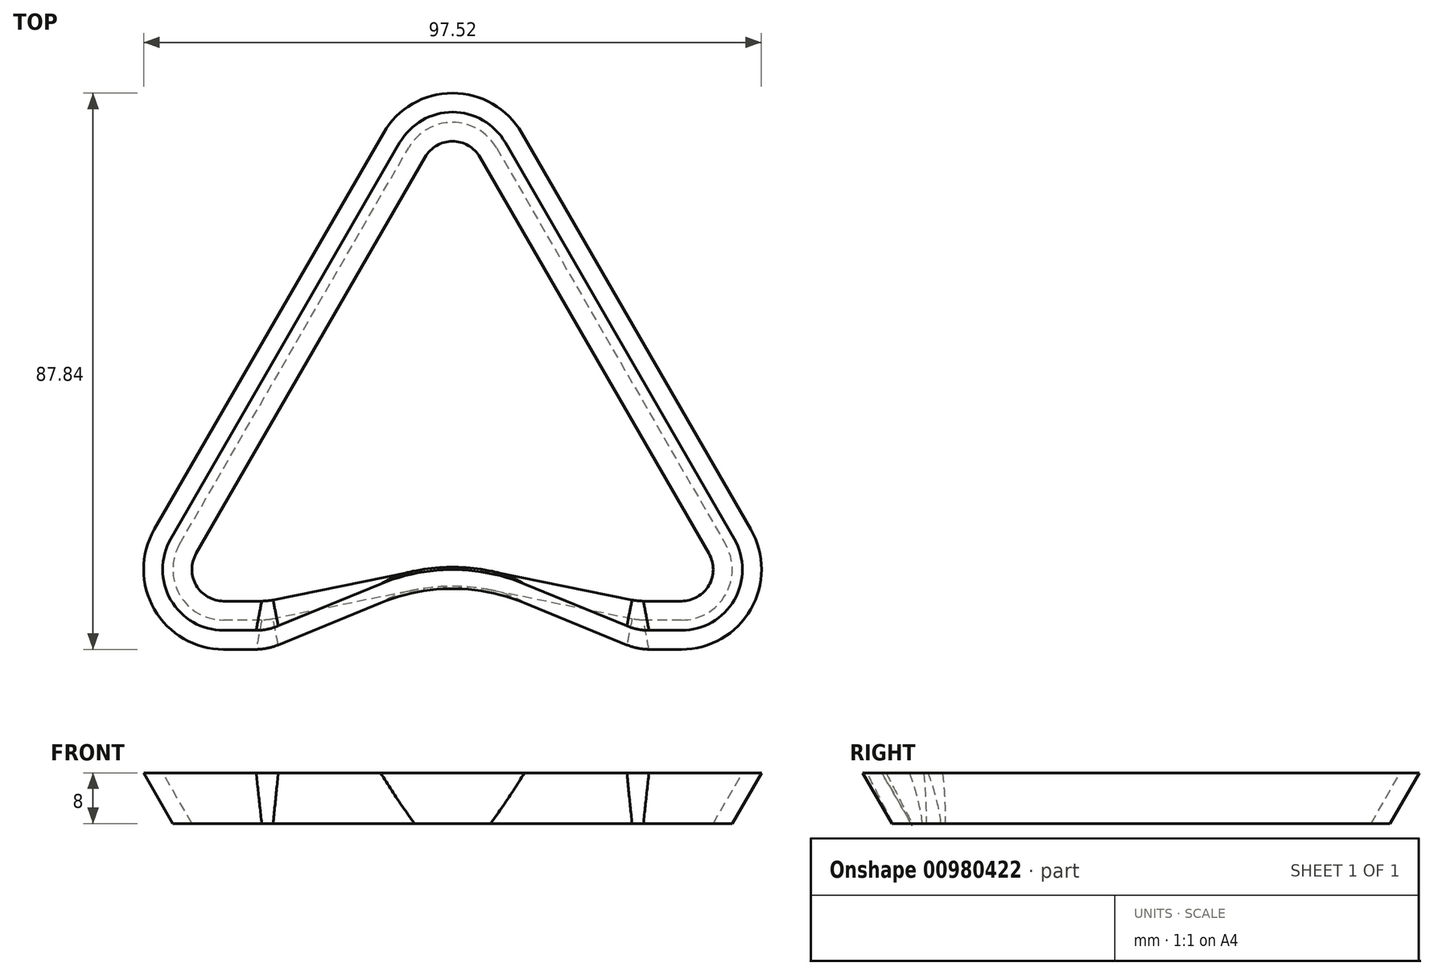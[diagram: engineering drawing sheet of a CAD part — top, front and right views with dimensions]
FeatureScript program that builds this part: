
annotation { "Feature Type Name" : "Feature", "Feature Type Description" : "" }
export const myFeature = defineFeature(function(context is Context, id is Id, definition is map)
    precondition{}
    {
        {
            var Q0;
            Q0=qCreatedBy(makeId("Top.planeOp"),FACE);
            var sketch = newSketch(context, id + "F0", { "sketchPlane" : qUnion([Q0])});
            skLineSegment(sketch, "E0", {"start": v(-50, 0) * mm, "end": v(50, 0) * mm, "construction": true});
            skLineSegment(sketch, "E1", {"start": v(50, 0) * mm, "end": v(0, 86.6) * mm, "construction": true});
            skLineSegment(sketch, "E2", {"start": v(0, 86.6) * mm, "end": v(-50, 0) * mm, "construction": true});
            skArc(sketch, "E3", {"start": v(-43.07, 12) * mm, "mid": v(-43.07, 4) * mm, "end": v(-36.14, 0) * mm});
            skArc(sketch, "E4", {"start": v(36.14, 0) * mm, "mid": v(43.07, 4) * mm, "end": v(43.07, 12) * mm});
            skArc(sketch, "E5", {"start": v(6.93, 74.6) * mm, "mid": v(0, 78.6) * mm, "end": v(-6.93, 74.6) * mm});
            skLineSegment(sketch, "E6", {"start": v(-43.07, 12) * mm, "end": v(-6.93, 74.6) * mm});
            skLineSegment(sketch, "E7", {"start": v(6.93, 74.6) * mm, "end": v(43.07, 12) * mm});
            skLineSegment(sketch, "E8", {"start": v(-36.14, 0) * mm, "end": v(-29.23, 0) * mm});
            skLineSegment(sketch, "E9", {"start": v(29.23, 0) * mm, "end": v(36.14, 0) * mm});
            skArc(sketch, "E10", {"start": v(3.3, 11.28) * mm, "mid": v(0, 12) * mm, "end": v(-3.3, 11.28) * mm});
            skLineSegment(sketch, "E11", {"start": v(-27.16, 0.45) * mm, "end": v(-3.3, 11.28) * mm});
            skLineSegment(sketch, "E12", {"start": v(3.3, 11.28) * mm, "end": v(27.16, 0.45) * mm});
            skPoint(sketch, "E13.visualSharp", {"position": v(-28.14, 0) * mm});
            skArc(sketch, "E13.filletArc", {"start": v(-29.23, 0) * mm, "mid": v(-28.17, 0.11) * mm, "end": v(-27.16, 0.45) * mm});
            skPoint(sketch, "E14.visualSharp", {"position": v(28.14, 0) * mm});
            skArc(sketch, "E14.filletArc", {"start": v(27.16, 0.45) * mm, "mid": v(28.17, 0.11) * mm, "end": v(29.23, 0) * mm});
            skLineSegment(sketch, "E15", {"start": v(-29.23, 0) * mm, "end": v(-29.23, 8) * mm, "construction": true});
            skSolve(sketch);
        }
        {
            var Q0;
            Q0=qCreatedBy(makeId("Right.planeOp"),FACE);
            var sketch = newSketch(context, id + "F1", { "sketchPlane" : qUnion([Q0])});
            skPoint(sketch, "E16.0", {"position": v(12, 0) * mm});
            skLineSegment(sketch, "E17", {"start": v(15, 0) * mm, "end": v(10.38, 8) * mm});
            skLineSegment(sketch, "E18", {"start": v(10.38, 8) * mm, "end": v(7.38, 8) * mm});
            skLineSegment(sketch, "E19", {"start": v(7.38, 8) * mm, "end": v(12, 0) * mm});
            skLineSegment(sketch, "E20", {"start": v(12, 0) * mm, "end": v(15, 0) * mm});
            skSolve(sketch);
        }
        {
            var Q0;
            Q0=sQuery(id+"F0.wireOp",EDGE,"E15");
            cPlane(context, id + "F2", {"entities" : qUnion([Q0]), "cplaneType" : CPlaneType.LINE_ANGLE, "offset" : 25 * mm, "angle" : 90 * degree, "width" : 150 * mm, "height" : 150 * mm});
        }
        {
            var Q0;
            Q0=qCreatedBy(id+"F2.planeOp",FACE);
            var sketch = newSketch(context, id + "F3", { "sketchPlane" : qUnion([Q0])});
            skLineSegment(sketch, "E21", {"start": v(0, 0) * mm, "end": v(-4.62, 8) * mm});
            skLineSegment(sketch, "E22", {"start": v(-4.62, 8) * mm, "end": v(-1.62, 8) * mm});
            skLineSegment(sketch, "E23", {"start": v(-1.62, 8) * mm, "end": v(3, 0) * mm});
            skLineSegment(sketch, "E24", {"start": v(3, 0) * mm, "end": v(0, 0) * mm});
            skSolve(sketch);
        }
        {
            var Q0;
            Q0=makeQuery(id+"F3.imprint","IMPRINT",FACE,{"disambiguationData":[TD([[makeQuery(id+"F3.imprint","IMPRINT",EDGE,{"derivedFrom":sQuery(id+"F3.wireOp",EDGE,"E21")}),-1.0]])]});
            var Q1;
            Q1=sQuery(id+"F0.wireOp",EDGE,"E8");
            var Q2;
            Q2=sQuery(id+"F0.wireOp",EDGE,"E3");
            var Q3;
            Q3=sQuery(id+"F0.wireOp",EDGE,"E6");
            var Q4;
            Q4=sQuery(id+"F0.wireOp",EDGE,"E5");
            var Q5;
            Q5=sQuery(id+"F0.wireOp",EDGE,"E7");
            var Q6;
            Q6=sQuery(id+"F0.wireOp",EDGE,"E4");
            var Q7;
            Q7=sQuery(id+"F0.wireOp",EDGE,"E9");
            sweep(context, id + "F4", {"profiles" : qUnion([Q0]), "path" : qUnion([Q1, Q2, Q3, Q4, Q5, Q6, Q7])});
        }
        {
            var Q0;
            Q0=qCreatedBy(makeId("Right.planeOp"),FACE);
            var sketch = newSketch(context, id + "F5", { "sketchPlane" : qUnion([Q0])});
            skLineSegment(sketch, "E25.0", {"start": v(10.38, 8) * mm, "end": v(7.38, 8) * mm});
            skLineSegment(sketch, "E26", {"start": v(10.38, 8) * mm, "end": v(8.97, 0) * mm});
            skLineSegment(sketch, "E27", {"start": v(8.97, 0) * mm, "end": v(5.97, 0) * mm});
            skLineSegment(sketch, "E28", {"start": v(5.97, 0) * mm, "end": v(7.38, 8) * mm});
            skSolve(sketch);
        }
        {
            var Q1;
            Q1=makeQuery(id+"F4.opSweep","CAP_FACE",FACE,{"disambiguationData":[OSD([sQuery(id+"F0.wireOp",VERTEX,"E13.filletArc.end"),sQuery(id+"F3.wireOp",EDGE,"E21"),sQuery(id+"F3.wireOp",EDGE,"E22"),sQuery(id+"F3.wireOp",EDGE,"E23"),sQuery(id+"F3.wireOp",EDGE,"E24")])],"isStart":false});
            var Q2;
            Q2=makeQuery(id+"F5.imprint","IMPRINT",FACE,{"disambiguationData":[TD([[makeQuery(id+"F5.imprint","IMPRINT",EDGE,{"derivedFrom":sQuery(id+"F5.wireOp",EDGE,"E25.0")}),1.0]])]});
            loft(context, id + "F6", {"operationType" : NewBodyOperationType.ADD, "sheetProfilesArray" : [{ "sheetProfileEntities" : qUnion([Q1]) }, { "sheetProfileEntities" : qUnion([Q2]) }]});
        }
        {
            var Q1;
            Q1=makeQuery(id+"F6.opLoft","CAP_FACE",FACE,{"disambiguationData":[OSD([makeQuery(id+"F5.imprint","IMPRINT",FACE,{"disambiguationData":[TD([[makeQuery(id+"F5.imprint","IMPRINT",EDGE,{"derivedFrom":sQuery(id+"F5.wireOp",EDGE,"E25.0")}),1.0]])]})])],"isStart":true});
            var Q2;
            Q2=makeQuery(id+"F4.opSweep","CAP_FACE",FACE,{"disambiguationData":[OSD([sQuery(id+"F0.wireOp",VERTEX,"E14.filletArc.start"),sQuery(id+"F3.wireOp",EDGE,"E21"),sQuery(id+"F3.wireOp",EDGE,"E22"),sQuery(id+"F3.wireOp",EDGE,"E23"),sQuery(id+"F3.wireOp",EDGE,"E24")])],"isStart":true});
            loft(context, id + "F7", {"operationType" : NewBodyOperationType.ADD, "sheetProfilesArray" : [{ "sheetProfileEntities" : qUnion([Q1]) }, { "sheetProfileEntities" : qUnion([Q2]) }]});
        }
        {
            var Q0;
            {var subQ0=sQuery(id+"F5.wireOp",EDGE,"E28");var subQ1=sQuery(id+"F5.wireOp",EDGE,"E27");var subQ2=sQuery(id+"F5.wireOp",EDGE,"E25.0");Q0=makeQuery(id+"F7.boolean.opBoolean","MERGE",EDGE,{"derivedFrom":[makeQuery(id+"F6.opLoft","MID_CAP_EDGE",EDGE,{"disambiguationData":[OSD([subQ2,subQ1,subQ0])],"capPos":1.0}),makeQuery(id+"F7.opLoft","MID_CAP_EDGE",EDGE,{"disambiguationData":[OSD([subQ2,subQ1,subQ0])],"capPos":0.0})]});}
            var Q1;
            {var subQ0=sQuery(id+"F5.wireOp",EDGE,"E27");var subQ1=sQuery(id+"F5.wireOp",EDGE,"E26");var subQ2=sQuery(id+"F5.wireOp",EDGE,"E25.0");Q1=makeQuery(id+"F7.boolean.opBoolean","MERGE",EDGE,{"derivedFrom":[makeQuery(id+"F6.opLoft","MID_CAP_EDGE",EDGE,{"disambiguationData":[OSD([subQ2,subQ1,subQ0])],"capPos":1.0}),makeQuery(id+"F7.opLoft","MID_CAP_EDGE",EDGE,{"disambiguationData":[OSD([subQ2,subQ1,subQ0])],"capPos":0.0})]});}
            fillet(context, id + "F8", {"entities" : qUnion([Q0, Q1]), "radius" : 30 * mm, "tangentPropagation" : true, "allowEdgeOverflow" : false});
        }
        {
            var Q0;
            {var subQ0=sQuery(id+"F3.wireOp",EDGE,"E21");var subQ1=sQuery(id+"F0.wireOp",VERTEX,"E8.end");Q0=makeQuery(id+"F7.boolean.opBoolean","MERGE",EDGE,{"derivedFrom":[makeQuery(id+"F4.opSweep","CAP_EDGE",EDGE,{"disambiguationData":[OSD([subQ1,subQ0])],"isStart":true}),makeQuery(id+"F7.opLoft","MID_CAP_EDGE",EDGE,{"disambiguationData":[OSD([subQ1,sQuery(id+"F0.wireOp",EDGE,"E8"),subQ0,sQuery(id+"F3.wireOp",EDGE,"E22"),sQuery(id+"F3.wireOp",EDGE,"E24")])],"capPos":1.0})]});}
            var Q1;
            {var subQ0=sQuery(id+"F3.wireOp",EDGE,"E23");var subQ1=sQuery(id+"F0.wireOp",VERTEX,"E8.end");Q1=makeQuery(id+"F7.boolean.opBoolean","MERGE",EDGE,{"derivedFrom":[makeQuery(id+"F4.opSweep","CAP_EDGE",EDGE,{"disambiguationData":[OSD([subQ1,subQ0])],"isStart":true}),makeQuery(id+"F7.opLoft","MID_CAP_EDGE",EDGE,{"disambiguationData":[OSD([subQ1,sQuery(id+"F0.wireOp",EDGE,"E8"),sQuery(id+"F3.wireOp",EDGE,"E22"),subQ0,sQuery(id+"F3.wireOp",EDGE,"E24")])],"capPos":1.0})]});}
            var Q2;
            {var subQ0=sQuery(id+"F3.wireOp",EDGE,"E23");var subQ1=sQuery(id+"F0.wireOp",VERTEX,"E9.start");Q2=makeQuery(id+"F6.boolean.opBoolean","MERGE",EDGE,{"derivedFrom":[makeQuery(id+"F4.opSweep","CAP_EDGE",EDGE,{"disambiguationData":[OSD([subQ1,subQ0])],"isStart":false}),makeQuery(id+"F6.opLoft","MID_CAP_EDGE",EDGE,{"disambiguationData":[OSD([subQ1,sQuery(id+"F0.wireOp",EDGE,"E9"),sQuery(id+"F3.wireOp",EDGE,"E22"),subQ0,sQuery(id+"F3.wireOp",EDGE,"E24")])],"capPos":0.0})]});}
            var Q3;
            {var subQ0=sQuery(id+"F3.wireOp",EDGE,"E21");var subQ1=sQuery(id+"F0.wireOp",VERTEX,"E9.start");Q3=makeQuery(id+"F6.boolean.opBoolean","MERGE",EDGE,{"derivedFrom":[makeQuery(id+"F4.opSweep","CAP_EDGE",EDGE,{"disambiguationData":[OSD([subQ1,subQ0])],"isStart":false}),makeQuery(id+"F6.opLoft","MID_CAP_EDGE",EDGE,{"disambiguationData":[OSD([subQ1,sQuery(id+"F0.wireOp",EDGE,"E9"),subQ0,sQuery(id+"F3.wireOp",EDGE,"E22"),sQuery(id+"F3.wireOp",EDGE,"E24")])],"capPos":0.0})]});}
            fillet(context, id + "F9", {"entities" : qUnion([Q0, Q1, Q2, Q3]), "radius" : 10 * mm, "tangentPropagation" : true, "allowEdgeOverflow" : false});
        }
    });
